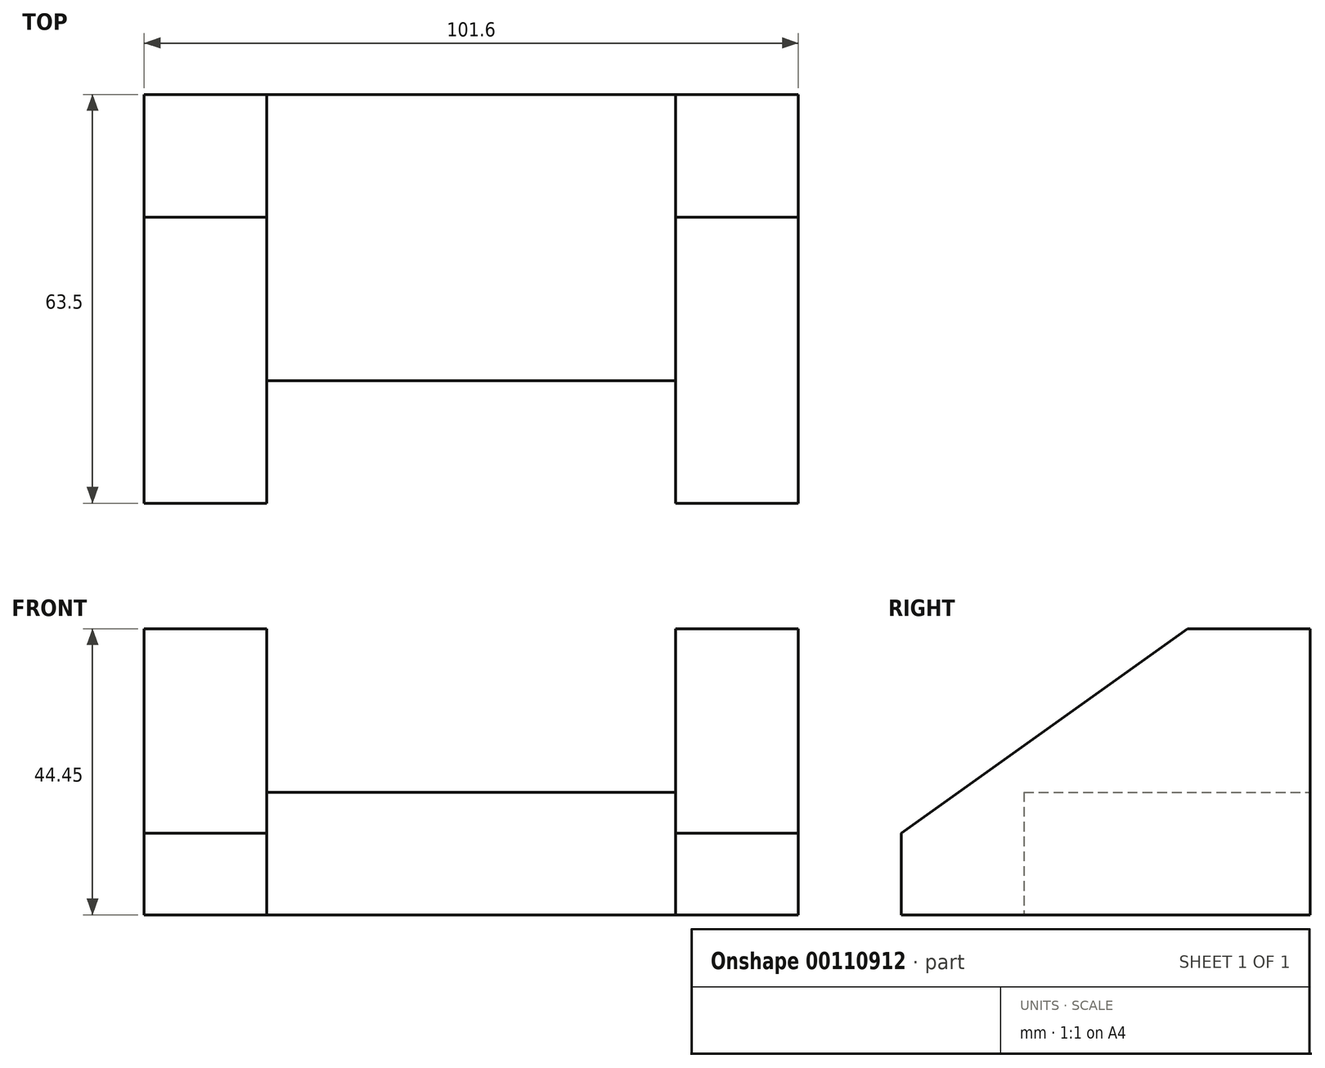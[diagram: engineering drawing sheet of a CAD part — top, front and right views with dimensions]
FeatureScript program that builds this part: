
annotation { "Feature Type Name" : "Feature", "Feature Type Description" : "" }
export const myFeature = defineFeature(function(context is Context, id is Id, definition is map)
    precondition{}
    {
        {
            var Q0;
            Q0=qCreatedBy(makeId("Top.planeOp"),FACE);
            var sketch = newSketch(context, id + "F0", { "sketchPlane" : qUnion([Q0])});
            skLineSegment(sketch, "E0", {"start": v(0, 0) * mm, "end": v(0, 63.5) * mm});
            skLineSegment(sketch, "E1", {"start": v(0, 63.5) * mm, "end": v(-101.6, 63.5) * mm});
            skLineSegment(sketch, "E2", {"start": v(-101.6, 63.5) * mm, "end": v(-101.6, 0) * mm});
            skLineSegment(sketch, "E3", {"start": v(-101.6, 0) * mm, "end": v(-82.55, 0) * mm});
            skLineSegment(sketch, "E4", {"start": v(-82.55, 0) * mm, "end": v(-82.55, 19.05) * mm});
            skLineSegment(sketch, "E5", {"start": v(-82.55, 19.05) * mm, "end": v(-19.05, 19.05) * mm});
            skLineSegment(sketch, "E6", {"start": v(-19.05, 19.05) * mm, "end": v(-19.05, 0) * mm});
            skLineSegment(sketch, "E7", {"start": v(-19.05, 0) * mm, "end": v(0, 0) * mm});
            skLineSegment(sketch, "E8", {"start": v(-82.55, 19.05) * mm, "end": v(-82.55, 63.5) * mm});
            skLineSegment(sketch, "E9", {"start": v(-19.05, 19.05) * mm, "end": v(-19.05, 63.5) * mm});
            skSolve(sketch);
        }
        {
            var Q0;
            Q0=makeQuery(id+"F0.imprint","IMPRINT",FACE,{"disambiguationData":[TD([[makeQuery(id+"F0.imprint","IMPRINT",EDGE,{"derivedFrom":sQuery(id+"F0.wireOp",EDGE,"E5")}),1.0]])]});
            extrude(context, id + "F1", {"entities" : qUnion([Q0]), "depth" : 19.05 * mm});
        }
        {
            var Q0;
            {var subQ1=sQuery(id+"F0.wireOp",EDGE,"E0");Q0=makeQuery(id+"F0.imprint","IMPRINT",FACE,{"disambiguationData":[TD([[makeQuery(id+"F0.imprint","IMPRINT",EDGE,{"derivedFrom":subQ1}),1.0]])]});}
            var Q1;
            {var subQ0=sQuery(id+"F0.wireOp",EDGE,"E2");Q1=makeQuery(id+"F0.imprint","IMPRINT",FACE,{"disambiguationData":[TD([[makeQuery(id+"F0.imprint","IMPRINT",EDGE,{"derivedFrom":subQ0}),1.0]])]});}
            extrude(context, id + "F2", {"entities" : qUnion([Q0, Q1]), "operationType" : NewBodyOperationType.ADD, "depth" : 44.45 * mm});
        }
        {
            var Q0;
            Q0=makeQuery(id+"F2.opExtrude","SWEPT_FACE",FACE,{"disambiguationData":[OSD([sQuery(id+"F0.wireOp",EDGE,"E0")])]});
            var sketch = newSketch(context, id + "F3", { "sketchPlane" : qUnion([Q0])});
            skLineSegment(sketch, "E10", {"start": v(44.45, 44.45) * mm, "end": v(0, 12.7) * mm});
            skSolve(sketch);
        }
        {
            var Q0;
            {var subQ0=sQuery(id+"F3.wireOp",EDGE,"E10");Q0=makeQuery(id+"F3.imprint","IMPRINT",FACE,{"disambiguationData":[TD([[makeQuery(id+"F3.imprint","IMPRINT",EDGE,{"derivedFrom":subQ0}),-1.0]])]});}
            extrude(context, id + "F4", {"entities" : qUnion([Q0]), "operationType" : NewBodyOperationType.REMOVE, "oppositeDirection" : true, "depth" : 101.6 * mm});
        }
    });
